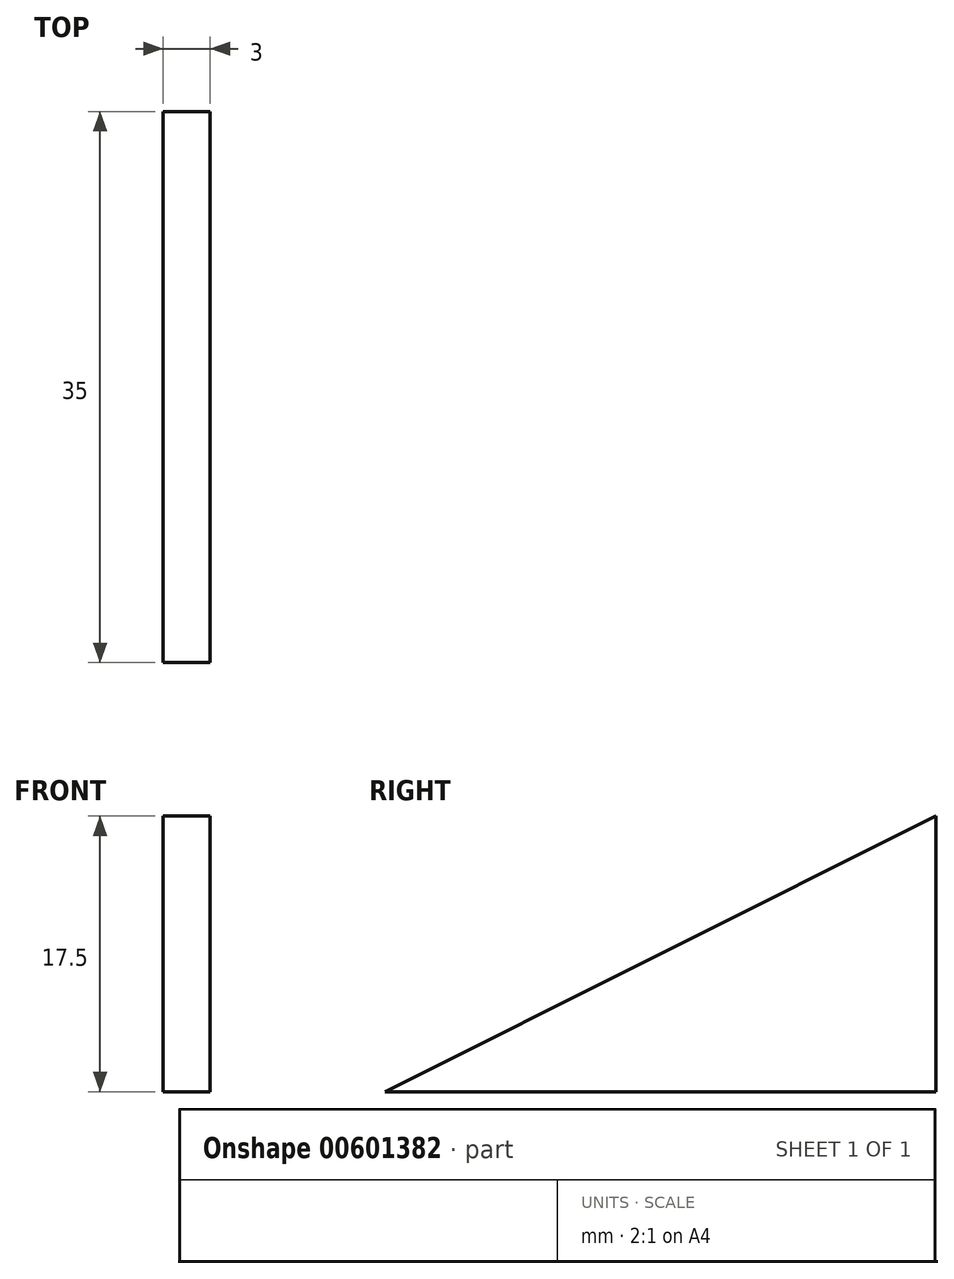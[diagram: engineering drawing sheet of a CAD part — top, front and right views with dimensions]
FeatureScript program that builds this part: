
annotation { "Feature Type Name" : "Feature", "Feature Type Description" : "" }
export const myFeature = defineFeature(function(context is Context, id is Id, definition is map)
    precondition{}
    {
        {
            var Q0;
            Q0=qCreatedBy(makeId("Right.planeOp"),FACE);
            var sketch = newSketch(context, id + "F0", { "sketchPlane" : qUnion([Q0])});
            skLineSegment(sketch, "E0.bottom", {"start": v(-17.5, -17.5) * mm, "end": v(17.5, -17.5) * mm});
            skLineSegment(sketch, "E0.top", {"start": v(-17.5, 17.5) * mm, "end": v(17.5, 17.5) * mm});
            skLineSegment(sketch, "E0.left", {"start": v(-17.5, -17.5) * mm, "end": v(-17.5, 17.5) * mm});
            skLineSegment(sketch, "E0.right", {"start": v(17.5, -17.5) * mm, "end": v(17.5, 17.5) * mm});
            skPoint(sketch, "E0.middle", {"position": v(0, 0) * mm});
            skFitSpline(sketch, "E1", {"points": [v(17.5, 0) * mm, v(-17.5, -17.5) * mm], "startDerivative": vector(-35, -17.5) * mm, "endDerivative": vector(-35, -17.5) * mm});
            skSolve(sketch);
        }
        {
            var Q0;
            Q0=makeQuery(id+"F0.imprint","IMPRINT",FACE,{"disambiguationData":[TD([[makeQuery(id+"F0.imprint","IMPRINT",EDGE,{"derivedFrom":sQuery(id+"F0.wireOp",EDGE,"E0.bottom")}),1.0]])]});
            extrude(context, id + "F1", {"entities" : qUnion([Q0]), "depth" : 3 * mm, "offsetDistance" : 25 * mm});
        }
    });
